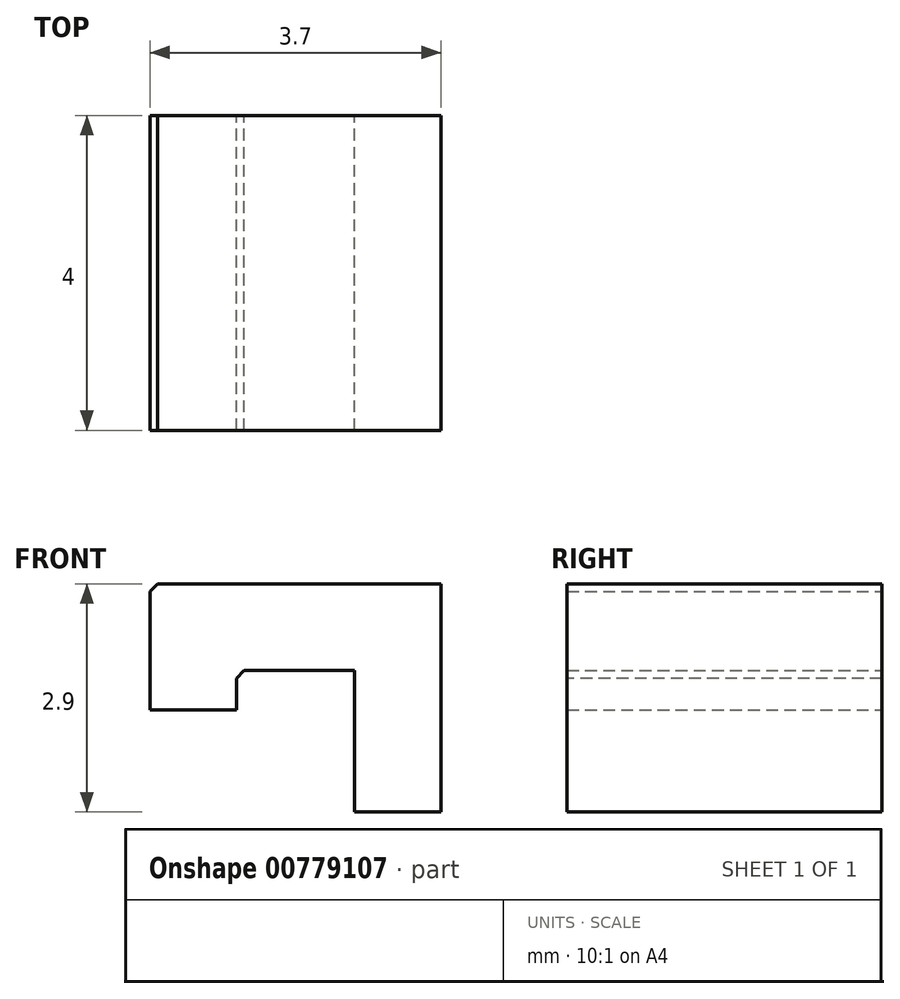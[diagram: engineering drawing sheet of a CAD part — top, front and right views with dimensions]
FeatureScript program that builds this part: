
annotation { "Feature Type Name" : "Feature", "Feature Type Description" : "" }
export const myFeature = defineFeature(function(context is Context, id is Id, definition is map)
    precondition{}
    {
        {
            var Q0;
            Q0=qCreatedBy(makeId("Front.planeOp"),FACE);
            var sketch = newSketch(context, id + "F0", { "sketchPlane" : qUnion([Q0])});
            skLineSegment(sketch, "E0", {"start": v(0, 0) * mm, "end": v(0, 0.5) * mm});
            skLineSegment(sketch, "E1", {"start": v(0, 0.5) * mm, "end": v(1.5, 0.5) * mm});
            skLineSegment(sketch, "E2", {"start": v(1.5, 0.5) * mm, "end": v(1.5, -1.3) * mm});
            skLineSegment(sketch, "E3", {"start": v(0, 0) * mm, "end": v(-1.1, 0) * mm});
            skLineSegment(sketch, "E4", {"start": v(-1.1, 0) * mm, "end": v(-1.1, 1.6) * mm});
            skLineSegment(sketch, "E5", {"start": v(1.5, -1.3) * mm, "end": v(2.6, -1.3) * mm});
            skLineSegment(sketch, "E6.0", {"start": v(-1.1, 1.6) * mm, "end": v(2.6, 1.6) * mm});
            skLineSegment(sketch, "E7", {"start": v(2.6, -1.3) * mm, "end": v(2.6, 1.6) * mm});
            skSolve(sketch);
        }
        {
            var Q0;
            Q0=makeQuery(id+"F0.imprint","IMPRINT",FACE,{"disambiguationData":[TD([[makeQuery(id+"F0.imprint","IMPRINT",EDGE,{"derivedFrom":sQuery(id+"F0.wireOp",EDGE,"E0")}),1.0]])]});
            extrude(context, id + "F1", {"entities" : qUnion([Q0]), "depth" : 4 * mm, "offsetDistance" : 25 * mm});
        }
        {
            var Q0;
            Q0=makeQuery(id+"F1.opExtrude","SWEPT_EDGE",EDGE,{"disambiguationData":[OSD([sQuery(id+"F0.wireOp",EDGE,"E0"),sQuery(id+"F0.wireOp",EDGE,"E1")])]});
            var Q1;
            Q1=makeQuery(id+"F1.opExtrude","SWEPT_EDGE",EDGE,{"disambiguationData":[OSD([sQuery(id+"F0.wireOp",EDGE,"E4"),sQuery(id+"F0.wireOp",EDGE,"E6.0")])]});
            chamfer(context, id + "F2", {"entities" : qUnion([Q0, Q1]), "width" : .1 * mm, "tangentPropagation" : true});
        }
    });
